# Revit family: NaughtOne_HatchSingleSeatLounge
name_source: partatom
category: Furniture
units: mm (PartAtom-declared; Revit-internal decimal feet)

## family parameters
Always vertical = Yes
Cut with Voids When Loaded = No
Enable Cutting in Views = No
Render Appearance Source = Family Geometry
Room Calculation Point = No
Shared = Yes
Work Plane-Based = No

## types (6) — shared parameters
Assembly Code = E2020200
AssetType = Moveable
BIMObjectName = Naughtone_Seating_Hatch
Category = Pr_40_50_12: Chairs, seats and benches
CodePerformance = PASSED BSEN 16139
Color = Various
DurationUnit = year
Export Type to IFC As = IfcFurnishingElementType
Finish = Upholstered
HasOneArmL = No
IfcExportAs = IfcFurnishingElementType
IfcExportType = SOFA
Is2Seat = No
Is3Seat = No
IsChair = No
LeftOffset = 255 mm  [stored 0.836614 ft]
MainColor = Various
ManufacturerAddressUK = naughtone, Knaresborough Tech Park, Manse Lane, Knaresborough, HG5 8LF
ManufacturerName = Naughtone
ManufacturerURL = www.naughtone.com
Material = Fabric, leather/steel/solid wood/beech ply/foam
ModelNumber = HAT1NA
ModelReference = Hatch Chair No Arms
NBSDescription = Seating
NBSReference = 45-35-72/352
Name = Seating_Hatch_Naughtone
NominalHeight = 685 mm  [stored 2.24738 ft]
NominalWidth = 690 mm  [stored 2.26378 ft]
Package Qty = 1
Product Documentation Link = http://www.naughtone.com
ProductInformation = www.naughtone.com/portfolio-view/hatch
RightOffset = 255 mm  [stored 0.836614 ft]
Shape = Rectangular
Size = 510x690x685mm
SustainabilityPerformance = FSC certified. FISP certified. ISO 14001 certified
Type IFC Predefined Type = SOFA
Uniclass2015Description = Chairs, seats and benches
Uniclass2015Reference = Pr_40_50_12
Uniclass2015Version = Products v1.5
Version = 1
VoidOffset2Seat = 10 mm  [stored 0.0328084 ft]
VoidOffset3Seat = 10 mm  [stored 0.0328084 ft]
VoidOffsetCentre = 255 mm  [stored 0.836614 ft]
WarrantyDurationLabor = 5
WarrantyDurationParts = 5
WarrantyDurationUnit = year
zero-valued in all types: Default Elevation

## per-type parameters (varying)
| type | Description | HasNoArms | HasOneArmR | HasTwoArms | Model |
| No Arms Single Fabric Lounge Ht | Hatch Single Seat Lounge No Arms lounge height 16 inch seat height Single Fabric | Yes | No | No | NOHAN120L1 |
| No Arms Multiple Fabric Lounge Ht | Hatch Single Seat No Arms Multiple lounge height 16 inch seat height Multiple Fabric | Yes | No | No | NOHAN120L2 |
| One Arm Corner Single Fabric Lounge Ht | Hatch Single Seat One Arm Corner Single lounge height 16 inch seat height Single Fabric | No | Yes | No | NOHAN130L1 |
| One Arm Corner Multiple Fabric Lounge Ht | Hatch Single Seat One Arm Corner Multiple lounge height 16 inch seat height Multiple Fabric | No | Yes | No | NOHAN130L2 |
| Two Arms Single Fabric Lounge Ht | Hatch Single Seat Two Arms Single lounge height 16 inch seat height Single Fabric | No | No | Yes | NOHAN140L1 |
| Two Arms Multiple Fabric Lounge Ht | Hatch Single Seat Two Arms Multiple lounge height 16 inch seat height Multiple Fabric | No | No | Yes | NOHAN140L2 |

note: [stored X ft] marks values corroborated as IEEE doubles in the binary element streams (Revit-internal decimal feet)

## geometry (parser evidence)
native form markers: Sweep x4
no freeform markers — native parametric forms only
